# Revit family: Kitchen_Sinks_hansgrohe_43340800-S4111-F340-Built-in-sink-340-40_
name_source: partatom
category: Plumbing Fixtures
revit_build: Autodesk Revit 2015 (Build: 20140903_1530(x64)
units: mm (PartAtom-declared; Revit-internal decimal feet)

## types (1)
- Stainless Steel
    BIMobject category = Sinks
    BIMobject category code = kitchen-sinks
    BIMobject main category = Kitchen
    BIMobject main category code = kitchen
    Brand url = http://www.hansgrohe-int.com
    Default Elevation = 4' - 0"
    Design country = Germany
    Edition number = 1
    GTIN code = https://4059625217450
    IFC Classification = Sanitary Terminal
    Installation instructions = https://www.hansgrohe.com
    Manufacturer country = Germany
    Manufacturer name = hansgrohe
    Material main = Chrome
    Product Guid = fd2429c7-16c5-4c45-8263-0814c2260aa2
    Product SKU = 43340800
    Product data url = https://bimobject.com
    Product family = S41
    Product group = Sinks
    Product name = 43340800 S4111-F340 Built-in sink 340/400 with drainboard
    Product url = https://www.hansgrohe.com
    QR code = http://bimobject.com
    Technical description = https://www.hansgrohe.com

## geometry (parser evidence)
native form markers: Sweep x3
no freeform markers — native parametric forms only
